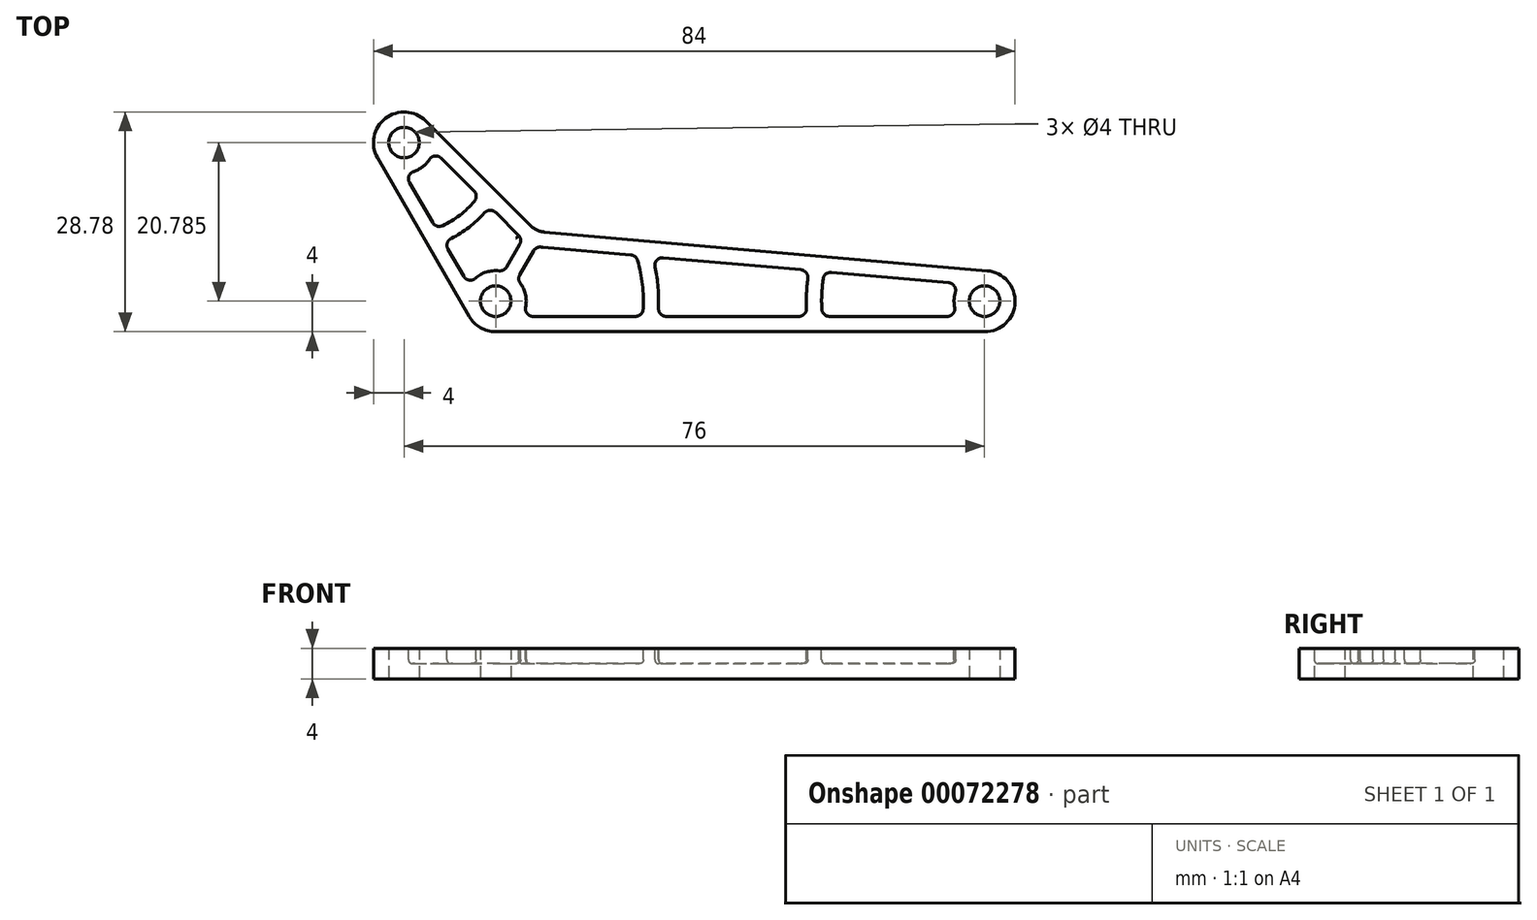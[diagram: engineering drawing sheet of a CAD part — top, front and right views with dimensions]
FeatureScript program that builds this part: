
annotation { "Feature Type Name" : "Feature", "Feature Type Description" : "" }
export const myFeature = defineFeature(function(context is Context, id is Id, definition is map)
    precondition{}
    {
        {
            assignVariable(context, id + "F0", {"name" : "HOLE", "anyValue" : 4});
        }
        {
            assignVariable(context, id + "F1", {"name" : "WALL", "anyValue" : 2});
        }
        {
            var Q0;
            Q0=qCreatedBy(makeId("Top.planeOp"),FACE);
            var sketch = newSketch(context, id + "F2", { "sketchPlane" : qUnion([Q0])});
            skCircle(sketch, "E0", {"center": v(0, 0) * mm, "radius": 4 * mm, "construction": true});
            skLineSegment(sketch, "E1", {"start": v(0, 0) * mm, "end": v(-12, 20.78) * mm, "construction": true});
            skLineSegment(sketch, "E2", {"start": v(0, 0) * mm, "end": v(64, 0) * mm, "construction": true});
            skCircle(sketch, "E3", {"center": v(-12, 20.78) * mm, "radius": 4 * mm, "construction": true});
            skCircle(sketch, "E4", {"center": v(64, 0) * mm, "radius": 4 * mm, "construction": true});
            skLineSegment(sketch, "E5", {"start": v(-8.54, 22.78) * mm, "end": v(3.46, 2) * mm, "construction": true});
            skLineSegment(sketch, "E6", {"start": v(-15.46, 18.78) * mm, "end": v(-3.46, -2) * mm});
            skArc(sketch, "E7", {"start": v(-8.54, 22.78) * mm, "mid": v(-14, 24.25) * mm, "end": v(-15.46, 18.78) * mm});
            skArc(sketch, "E8", {"start": v(64, -4) * mm, "mid": v(68, 0) * mm, "end": v(64, 4) * mm});
            skArc(sketch, "E9", {"start": v(-3.46, -2) * mm, "mid": v(-2, -3.46) * mm, "end": v(0, -4) * mm});
            skCircle(sketch, "E10", {"center": v(-12, 20.78) * mm, "radius": 2 * mm});
            skCircle(sketch, "E11", {"center": v(0, 0) * mm, "radius": 2 * mm});
            skCircle(sketch, "E12", {"center": v(64, 0) * mm, "radius": 2 * mm});
            skLineSegment(sketch, "E13", {"start": v(0, -4) * mm, "end": v(64, -4) * mm});
            skLineSegment(sketch, "E14", {"start": v(64, 4) * mm, "end": v(0, 4) * mm, "construction": true});
            skPoint(sketch, "E15", {"position": v(2.3, 4) * mm});
            skLineSegment(sketch, "E16", {"start": v(-8.54, 22.78) * mm, "end": v(2.3, 4) * mm});
            skLineSegment(sketch, "E17", {"start": v(2.3, 4) * mm, "end": v(64, 4) * mm});
            skLineSegment(sketch, "E18", {"start": v(0, 0) * mm, "end": v(2.3, 4) * mm, "construction": true});
            skSolve(sketch);
        }
        {
            var Q0;
            Q0=qCreatedBy(makeId("Top.planeOp"),FACE);
            var sketch = newSketch(context, id + "F3", { "sketchPlane" : qUnion([Q0])});
            skLineSegment(sketch, "E19.2", {"start": v(-13.73, 19.78) * mm, "end": v(-1.73, -1) * mm});
            skArc(sketch, "E19.3", {"start": v(-1.73, -1) * mm, "mid": v(-1, -1.73) * mm, "end": v(0, -2) * mm});
            skLineSegment(sketch, "E19.4", {"start": v(0, -2) * mm, "end": v(64, -2) * mm});
            skArc(sketch, "E19.5", {"start": v(-10.59, 22.2) * mm, "mid": v(-13.22, 22.37) * mm, "end": v(-13.73, 19.78) * mm});
            skArc(sketch, "E19.6", {"start": v(64, -2) * mm, "mid": v(66, -0.09) * mm, "end": v(64.17, 2) * mm});
            skLineSegment(sketch, "E20.0", {"start": v(-15.46, 18.78) * mm, "end": v(-3.46, -2) * mm});
            skLineSegment(sketch, "E20.5", {"start": v(0, -4) * mm, "end": v(64, -4) * mm});
            skArc(sketch, "E20.6", {"start": v(-3.46, -2) * mm, "mid": v(-2, -3.46) * mm, "end": v(0, -4) * mm});
            skLineSegment(sketch, "E21", {"start": v(-9.17, 23.61) * mm, "end": v(4.51, 9.93) * mm});
            skLineSegment(sketch, "E22", {"start": v(6.37, 9.06) * mm, "end": v(64.35, 3.98) * mm});
            skArc(sketch, "E23", {"start": v(-9.17, 23.61) * mm, "mid": v(-14.44, 23.96) * mm, "end": v(-15.46, 18.78) * mm});
            skArc(sketch, "E24", {"start": v(64, -4) * mm, "mid": v(68, -0.17) * mm, "end": v(64.35, 3.98) * mm});
            skLineSegment(sketch, "E25", {"start": v(0, 0) * mm, "end": v(9.01, 15.61) * mm, "construction": true});
            skPoint(sketch, "E26.visualSharp", {"position": v(5.29, 9.16) * mm});
            skArc(sketch, "E26.filletArc", {"start": v(4.51, 9.93) * mm, "mid": v(5.37, 9.33) * mm, "end": v(6.37, 9.06) * mm});
            skLineSegment(sketch, "E27.0", {"start": v(6.2, 7.07) * mm, "end": v(64.17, 2) * mm});
            skArc(sketch, "E27.1", {"start": v(3.1, 8.51) * mm, "mid": v(4.52, 7.52) * mm, "end": v(6.2, 7.07) * mm});
            skLineSegment(sketch, "E27.2", {"start": v(-10.59, 22.2) * mm, "end": v(3.1, 8.51) * mm});
            skSolve(sketch);
        }
        {
            var Q0;
            Q0=qCreatedBy(makeId("Top.planeOp"),FACE);
            var sketch = newSketch(context, id + "F4", { "sketchPlane" : qUnion([Q0])});
            skLineSegment(sketch, "E28", {"start": v(-11.28, 15.54) * mm, "end": v(-4.18, 3.24) * mm});
            skLineSegment(sketch, "E29", {"start": v(-7.12, 18.73) * mm, "end": v(3.1, 8.51) * mm});
            skLineSegment(sketch, "E30", {"start": v(6.2, 7.07) * mm, "end": v(59.3, 2.42) * mm});
            skLineSegment(sketch, "E31", {"start": v(59.1, -2) * mm, "end": v(4.9, -2) * mm});
            skLineSegment(sketch, "E32", {"start": v(1.43, 4.47) * mm, "end": v(3.14, 7.43) * mm});
            skLineSegment(sketch, "E33", {"start": v(3.16, 3.47) * mm, "end": v(4.97, 6.6) * mm});
            skArc(sketch, "E34", {"start": v(-10.73, 17) * mm, "mid": v(-9.56, 17.61) * mm, "end": v(-8.66, 18.58) * mm});
            skArc(sketch, "E35", {"start": v(0.45, 3.97) * mm, "mid": v(-1.2, 3.81) * mm, "end": v(-2.65, 3) * mm});
            skArc(sketch, "E36", {"start": v(3.92, -0.8) * mm, "mid": v(3.9, 0.86) * mm, "end": v(3.22, 2.37) * mm});
            skArc(sketch, "E37", {"start": v(60.17, 1.14) * mm, "mid": v(60, 0.17) * mm, "end": v(60.08, -0.8) * mm});
            skArc(sketch, "E38", {"start": v(3.1, 8.51) * mm, "mid": v(10.22, 15.53) * mm, "end": v(3, 8.62) * mm});
            skArc(sketch, "E39", {"start": v(5.97, 7.1) * mm, "mid": v(6.08, 7.08) * mm, "end": v(6.2, 7.07) * mm});
            skPoint(sketch, "E40.visualSharp", {"position": v(3.54, 8.13) * mm});
            skArc(sketch, "E40.filletArc", {"start": v(3.14, 7.43) * mm, "mid": v(3.26, 8.05) * mm, "end": v(3, 8.62) * mm});
            skPoint(sketch, "E41.visualSharp", {"position": v(5.33, 7.22) * mm});
            skArc(sketch, "E41.filletArc", {"start": v(5.97, 7.1) * mm, "mid": v(5.4, 7) * mm, "end": v(4.97, 6.6) * mm});
            skLineSegment(sketch, "E42", {"start": v(64, 0) * mm, "end": v(-8.36, 3.16) * mm, "construction": true});
            skCircle(sketch, "E43", {"center": v(-12, 20.78) * mm, "radius": 12 * mm, "construction": true});
            skPoint(sketch, "E44.visualSharp", {"position": v(-13.04, 24.65) * mm});
            skArc(sketch, "E44.filletArc", {"start": v(-7.12, 18.73) * mm, "mid": v(-7.93, 19.02) * mm, "end": v(-8.66, 18.58) * mm});
            skPoint(sketch, "E45.visualSharp", {"position": v(-12, 16.78) * mm});
            skArc(sketch, "E45.filletArc", {"start": v(-10.73, 17) * mm, "mid": v(-11.35, 16.4) * mm, "end": v(-11.28, 15.54) * mm});
            skPoint(sketch, "E46.visualSharp", {"position": v(1.07, 3.85) * mm});
            skArc(sketch, "E46.filletArc", {"start": v(0.45, 3.97) * mm, "mid": v(1, 4.08) * mm, "end": v(1.43, 4.47) * mm});
            skPoint(sketch, "E47.visualSharp", {"position": v(-3.46, 2) * mm});
            skArc(sketch, "E47.filletArc", {"start": v(-4.18, 3.24) * mm, "mid": v(-3.48, 2.76) * mm, "end": v(-2.65, 3) * mm});
            skPoint(sketch, "E48.visualSharp", {"position": v(2.8, 2.85) * mm});
            skArc(sketch, "E48.filletArc", {"start": v(3.16, 3.47) * mm, "mid": v(3.02, 2.91) * mm, "end": v(3.22, 2.37) * mm});
            skPoint(sketch, "E49.visualSharp", {"position": v(3.46, -2) * mm});
            skArc(sketch, "E49.filletArc", {"start": v(3.92, -0.8) * mm, "mid": v(4.12, -1.63) * mm, "end": v(4.9, -2) * mm});
            skPoint(sketch, "E50.visualSharp", {"position": v(60.72, 2.3) * mm});
            skArc(sketch, "E50.filletArc", {"start": v(60.17, 1.14) * mm, "mid": v(60.03, 1.99) * mm, "end": v(59.3, 2.42) * mm});
            skPoint(sketch, "E51.visualSharp", {"position": v(60.54, -2) * mm});
            skArc(sketch, "E51.filletArc", {"start": v(59.1, -2) * mm, "mid": v(59.88, -1.63) * mm, "end": v(60.08, -0.8) * mm});
            skLineSegment(sketch, "E52", {"start": v(-12, 20.78) * mm, "end": v(10, -7.88) * mm, "construction": true});
            skPoint(sketch, "E53", {"position": v(-9.56, 17.61) * mm});
            skArc(sketch, "E54", {"start": v(-7.82, 9.54) * mm, "mid": v(-4.7, 11.26) * mm, "end": v(-2.22, 13.83) * mm});
            skArc(sketch, "E55", {"start": v(-6.8, 7.78) * mm, "mid": v(-3.48, 9.68) * mm, "end": v(-0.79, 12.4) * mm});
            skArc(sketch, "E56", {"start": v(21.24, -2) * mm, "mid": v(21.12, 3.03) * mm, "end": v(19.82, 7.88) * mm});
            skArc(sketch, "E57", {"start": v(43.02, 3.84) * mm, "mid": v(42.69, 0.93) * mm, "end": v(42.76, -2) * mm});
            skArc(sketch, "E58", {"start": v(19.23, -2) * mm, "mid": v(17.22, 8.79) * mm, "end": v(9.67, 16.74) * mm});
            skArc(sketch, "E59", {"start": v(41.02, 4.02) * mm, "mid": v(40.69, 1.02) * mm, "end": v(40.75, -2) * mm});
            skSolve(sketch);
        }
        {
            var Q0;
            Q0=makeQuery(id+"F3.imprint","IMPRINT",FACE,{"disambiguationData":[TD([[makeQuery(id+"F3.imprint","IMPRINT",EDGE,{"derivedFrom":sQuery(id+"F3.wireOp",EDGE,"E19.2")}),1.0]])]});
            var Q1;
            Q1=makeQuery(id+"F3.imprint","IMPRINT",FACE,{"disambiguationData":[TD([[makeQuery(id+"F3.imprint","IMPRINT",EDGE,{"derivedFrom":sQuery(id+"F3.wireOp",EDGE,"E19.2")}),-1.0]])]});
            extrude(context, id + "F5", {"entities" : qUnion([Q0, Q1]), "oppositeDirection" : true, "depth" : (getVariable(context, 'WALL') * 2) * mm});
        }
        {
            var Q0;
            {var subQ5=sQuery(id+"F4.wireOp",EDGE,"E34");Q0=makeQuery(id+"F4.imprint","IMPRINT",FACE,{"disambiguationData":[TD([[makeQuery(id+"F4.imprint","IMPRINT",EDGE,{"derivedFrom":subQ5}),-1.0]])]});}
            var Q1;
            {var subQ5=sQuery(id+"F4.wireOp",EDGE,"E37");Q1=makeQuery(id+"F4.imprint","IMPRINT",FACE,{"disambiguationData":[TD([[makeQuery(id+"F4.imprint","IMPRINT",EDGE,{"derivedFrom":subQ5}),-1.0]])]});}
            var Q2;
            Q2=makeQuery(id+"F4.imprint","IMPRINT",FACE,{"disambiguationData":[TD([[makeQuery(id+"F4.imprint","IMPRINT",EDGE,{"derivedFrom":sQuery(id+"F4.wireOp",EDGE,"E35")}),-1.0]])]});
            var Q3;
            Q3=makeQuery(id+"F4.imprint","IMPRINT",FACE,{"disambiguationData":[TD([[makeQuery(id+"F4.imprint","IMPRINT",EDGE,{"derivedFrom":sQuery(id+"F4.wireOp",EDGE,"E36")}),-1.0]])]});
            var Q4;
            {var subQ3=sQuery(id+"F4.wireOp",EDGE,"E39");Q4=makeQuery(id+"F4.imprint","IMPRINT",FACE,{"disambiguationData":[TD([[makeQuery(id+"F4.imprint","IMPRINT",EDGE,{"derivedFrom":subQ3}),-1.0]])]});}
            var Q5;
            {var subQ5=sQuery(id+"F4.wireOp",EDGE,"E59");Q5=makeQuery(id+"F4.imprint","IMPRINT",FACE,{"disambiguationData":[TD([[makeQuery(id+"F4.imprint","IMPRINT",EDGE,{"derivedFrom":subQ5}),-1.0]])]});}
            extrude(context, id + "F6", {"entities" : qUnion([Q0, Q1, Q2, Q3, Q4, Q5]), "operationType" : NewBodyOperationType.REMOVE, "oppositeDirection" : true, "depth" : (getVariable(context, 'WALL')) * mm});
        }
        {
            var Q0;
            Q0=makeQuery(id+"F6.boolean.opBoolean","COPY",EDGE,{"derivedFrom":makeQuery(id+"F6.opExtrude","SWEPT_EDGE",EDGE,{"disambiguationData":[OSD([sQuery(id+"F4.wireOp",EDGE,"E28"),sQuery(id+"F4.wireOp",EDGE,"E55")])]})});
            var Q1;
            Q1=makeQuery(id+"F6.boolean.opBoolean","COPY",EDGE,{"derivedFrom":makeQuery(id+"F6.opExtrude","SWEPT_EDGE",EDGE,{"disambiguationData":[OSD([sQuery(id+"F4.wireOp",EDGE,"E29"),sQuery(id+"F4.wireOp",EDGE,"E55")])]})});
            var Q2;
            Q2=makeQuery(id+"F6.boolean.opBoolean","COPY",EDGE,{"derivedFrom":makeQuery(id+"F6.opExtrude","SWEPT_EDGE",EDGE,{"disambiguationData":[OSD([sQuery(id+"F4.wireOp",EDGE,"E28"),sQuery(id+"F4.wireOp",EDGE,"E54")])]})});
            var Q3;
            Q3=makeQuery(id+"F6.boolean.opBoolean","COPY",EDGE,{"derivedFrom":makeQuery(id+"F6.opExtrude","SWEPT_EDGE",EDGE,{"disambiguationData":[OSD([sQuery(id+"F4.wireOp",EDGE,"E29"),sQuery(id+"F4.wireOp",EDGE,"E54")])]})});
            var Q4;
            Q4=makeQuery(id+"F6.boolean.opBoolean","COPY",EDGE,{"derivedFrom":makeQuery(id+"F6.opExtrude","SWEPT_EDGE",EDGE,{"disambiguationData":[OSD([sQuery(id+"F4.wireOp",EDGE,"E33"),sQuery(id+"F4.wireOp",EDGE,"E58")])]})});
            var Q5;
            Q5=makeQuery(id+"F6.boolean.opBoolean","COPY",EDGE,{"derivedFrom":makeQuery(id+"F6.opExtrude","SWEPT_EDGE",EDGE,{"disambiguationData":[OSD([sQuery(id+"F4.wireOp",EDGE,"E31"),sQuery(id+"F4.wireOp",EDGE,"E58")])]})});
            var Q6;
            Q6=makeQuery(id+"F6.boolean.opBoolean","COPY",EDGE,{"derivedFrom":makeQuery(id+"F6.opExtrude","SWEPT_EDGE",EDGE,{"disambiguationData":[OSD([sQuery(id+"F4.wireOp",EDGE,"E33"),sQuery(id+"F4.wireOp",EDGE,"E56")])]})});
            var Q7;
            Q7=makeQuery(id+"F6.boolean.opBoolean","COPY",EDGE,{"derivedFrom":makeQuery(id+"F6.opExtrude","SWEPT_EDGE",EDGE,{"disambiguationData":[OSD([sQuery(id+"F4.wireOp",EDGE,"E31"),sQuery(id+"F4.wireOp",EDGE,"E56")])]})});
            var Q8;
            Q8=makeQuery(id+"F6.boolean.opBoolean","COPY",EDGE,{"derivedFrom":makeQuery(id+"F6.opExtrude","SWEPT_EDGE",EDGE,{"disambiguationData":[OSD([sQuery(id+"F4.wireOp",EDGE,"E30"),sQuery(id+"F4.wireOp",EDGE,"E59")])]})});
            var Q9;
            Q9=makeQuery(id+"F6.boolean.opBoolean","COPY",EDGE,{"derivedFrom":makeQuery(id+"F6.opExtrude","SWEPT_EDGE",EDGE,{"disambiguationData":[OSD([sQuery(id+"F4.wireOp",EDGE,"E31"),sQuery(id+"F4.wireOp",EDGE,"E59")])]})});
            var Q10;
            Q10=makeQuery(id+"F6.boolean.opBoolean","COPY",EDGE,{"derivedFrom":makeQuery(id+"F6.opExtrude","SWEPT_EDGE",EDGE,{"disambiguationData":[OSD([sQuery(id+"F4.wireOp",EDGE,"E30"),sQuery(id+"F4.wireOp",EDGE,"E57")])]})});
            var Q11;
            Q11=makeQuery(id+"F6.boolean.opBoolean","COPY",EDGE,{"derivedFrom":makeQuery(id+"F6.opExtrude","SWEPT_EDGE",EDGE,{"disambiguationData":[OSD([sQuery(id+"F4.wireOp",EDGE,"E31"),sQuery(id+"F4.wireOp",EDGE,"E57")])]})});
            fillet(context, id + "F7", {"entities" : qUnion([Q0, Q1, Q2, Q3, Q4, Q5, Q6, Q7, Q8, Q9, Q10, Q11]), "radius" : (getVariable(context, 'WALL') / 2) * mm, "tangentPropagation" : true, "allowEdgeOverflow" : false});
        }
        {
            var Q0;
            Q0=sQuery(id+"F3.wireOp",VERTEX,"E19.5.center");
            var Q1;
            Q1=sQuery(id+"F4.wireOp",VERTEX,"E37.center");
            var Q2;
            Q2=sQuery(id+"F3.wireOp",VERTEX,"E19.3.center");
            var Q3;
            Q3=makeQuery(id+"F5.opExtrude","SWEPT_BODY",BODY,{"disambiguationData":[OSD([sQuery(id+"F3.wireOp",EDGE,"E20.0"),sQuery(id+"F3.wireOp",EDGE,"E20.5"),sQuery(id+"F3.wireOp",EDGE,"E20.6"),sQuery(id+"F3.wireOp",EDGE,"E21"),sQuery(id+"F3.wireOp",EDGE,"E22"),sQuery(id+"F3.wireOp",EDGE,"E23"),sQuery(id+"F3.wireOp",EDGE,"E24"),sQuery(id+"F3.wireOp",EDGE,"E26.filletArc")])]});
            hole(context, id + "F8", {"style" : HoleStyle.SIMPLE, "holeDiameter" : (getVariable(context, 'HOLE')) * mm, "endStyle" : HoleEndStyle.THROUGH, "locations" : qUnion([Q0, Q1, Q2]), "scope" : qUnion([Q3])});
        }
        {
            var Q0;
            Q0=makeQuery(id+"F6.boolean.opBoolean","COPY",FACE,{"derivedFrom":makeQuery(id+"F6.opExtrude","CAP_FACE",FACE,{"disambiguationData":[OSD([sQuery(id+"F4.wireOp",EDGE,"E28"),sQuery(id+"F4.wireOp",EDGE,"E29"),sQuery(id+"F4.wireOp",EDGE,"E32"),sQuery(id+"F4.wireOp",EDGE,"E34"),sQuery(id+"F4.wireOp",EDGE,"E38"),sQuery(id+"F4.wireOp",EDGE,"E40.filletArc"),sQuery(id+"F4.wireOp",EDGE,"E44.filletArc"),sQuery(id+"F4.wireOp",EDGE,"E45.filletArc"),sQuery(id+"F4.wireOp",EDGE,"E54")])],"isStart":false})});
            var Q1;
            Q1=makeQuery(id+"F6.boolean.opBoolean","COPY",FACE,{"derivedFrom":makeQuery(id+"F6.opExtrude","CAP_FACE",FACE,{"disambiguationData":[OSD([sQuery(id+"F4.wireOp",EDGE,"E28"),sQuery(id+"F4.wireOp",EDGE,"E32"),sQuery(id+"F4.wireOp",EDGE,"E35"),sQuery(id+"F4.wireOp",EDGE,"E46.filletArc"),sQuery(id+"F4.wireOp",EDGE,"E47.filletArc"),sQuery(id+"F4.wireOp",EDGE,"E55")])],"isStart":false})});
            var Q2;
            Q2=makeQuery(id+"F6.boolean.opBoolean","COPY",FACE,{"derivedFrom":makeQuery(id+"F6.opExtrude","CAP_FACE",FACE,{"disambiguationData":[OSD([sQuery(id+"F4.wireOp",EDGE,"E31"),sQuery(id+"F4.wireOp",EDGE,"E33"),sQuery(id+"F4.wireOp",EDGE,"E36"),sQuery(id+"F4.wireOp",EDGE,"E48.filletArc"),sQuery(id+"F4.wireOp",EDGE,"E49.filletArc"),sQuery(id+"F4.wireOp",EDGE,"E58")])],"isStart":false})});
            var Q3;
            Q3=makeQuery(id+"F6.boolean.opBoolean","COPY",FACE,{"derivedFrom":makeQuery(id+"F6.opExtrude","CAP_FACE",FACE,{"disambiguationData":[OSD([sQuery(id+"F4.wireOp",EDGE,"E30"),sQuery(id+"F4.wireOp",EDGE,"E31"),sQuery(id+"F4.wireOp",EDGE,"E33"),sQuery(id+"F4.wireOp",EDGE,"E39"),sQuery(id+"F4.wireOp",EDGE,"E41.filletArc"),sQuery(id+"F4.wireOp",EDGE,"E56"),sQuery(id+"F4.wireOp",EDGE,"E59")])],"isStart":false})});
            var Q4;
            Q4=makeQuery(id+"F6.boolean.opBoolean","COPY",FACE,{"derivedFrom":makeQuery(id+"F6.opExtrude","CAP_FACE",FACE,{"disambiguationData":[OSD([sQuery(id+"F4.wireOp",EDGE,"E30"),sQuery(id+"F4.wireOp",EDGE,"E31"),sQuery(id+"F4.wireOp",EDGE,"E37"),sQuery(id+"F4.wireOp",EDGE,"E50.filletArc"),sQuery(id+"F4.wireOp",EDGE,"E51.filletArc"),sQuery(id+"F4.wireOp",EDGE,"E57")])],"isStart":false})});
            fillet(context, id + "F9", {"entities" : qUnion([Q0, Q1, Q2, Q3, Q4]), "radius" : (getVariable(context, 'WALL') / 4) * mm, "tangentPropagation" : true, "allowEdgeOverflow" : false});
        }
    });
